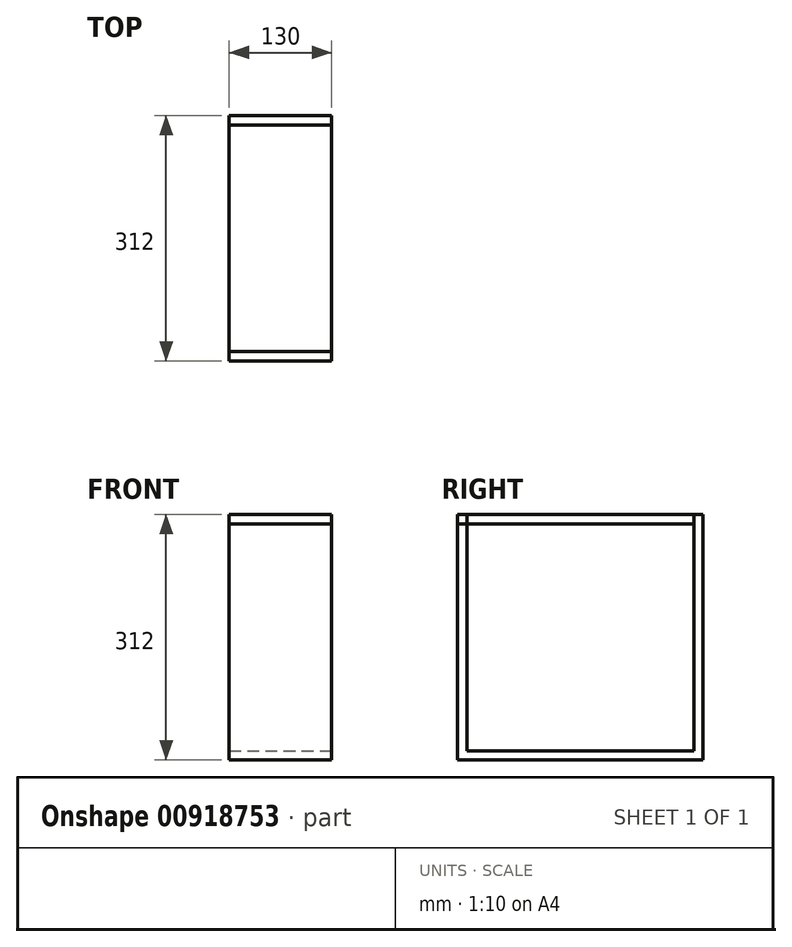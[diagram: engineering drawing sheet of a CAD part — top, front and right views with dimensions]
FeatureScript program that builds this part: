
annotation { "Feature Type Name" : "Feature", "Feature Type Description" : "" }
export const myFeature = defineFeature(function(context is Context, id is Id, definition is map)
    precondition{}
    {
        {
            var Q0;
            Q0=qCreatedBy(makeId("Top.planeOp"),FACE);
            var sketch = newSketch(context, id + "F0", { "sketchPlane" : qUnion([Q0])});
            skLineSegment(sketch, "E0.bottom", {"start": v(-937.94, -1757.44) * mm, "end": v(-807.94, -1757.44) * mm});
            skLineSegment(sketch, "E0.top", {"start": v(-937.94, -1769.44) * mm, "end": v(-807.94, -1769.44) * mm});
            skLineSegment(sketch, "E0.left", {"start": v(-937.94, -1757.44) * mm, "end": v(-937.94, -1769.44) * mm});
            skLineSegment(sketch, "E0.right", {"start": v(-807.94, -1757.44) * mm, "end": v(-807.94, -1769.44) * mm});
            skLineSegment(sketch, "E1.bottom", {"start": v(-937.94, -1469.44) * mm, "end": v(-807.94, -1469.44) * mm});
            skLineSegment(sketch, "E1.top", {"start": v(-937.94, -1457.44) * mm, "end": v(-807.94, -1457.44) * mm});
            skLineSegment(sketch, "E1.left", {"start": v(-937.94, -1457.44) * mm, "end": v(-937.94, -1469.44) * mm});
            skLineSegment(sketch, "E1.right", {"start": v(-807.94, -1457.44) * mm, "end": v(-807.94, -1469.44) * mm});
            skSolve(sketch);
        }
        {
            var Q0;
            Q0=makeQuery(id+"F0.imprint","IMPRINT",FACE,{"disambiguationData":[TD([[makeQuery(id+"F0.imprint","IMPRINT",EDGE,{"derivedFrom":sQuery(id+"F0.wireOp",EDGE,"E0.bottom")}),-1.0]])]});
            var Q1;
            Q1=makeQuery(id+"F0.imprint","IMPRINT",FACE,{"disambiguationData":[TD([[makeQuery(id+"F0.imprint","IMPRINT",EDGE,{"derivedFrom":sQuery(id+"F0.wireOp",EDGE,"E1.bottom")}),1.0]])]});
            extrude(context, id + "F1", {"entities" : qUnion([Q0, Q1]), "depth" : 300 * mm, "offsetDistance" : 25 * mm});
        }
        {
            var Q0;
            Q0=makeQuery(id+"F1.opExtrude","SWEPT_FACE",FACE,{"disambiguationData":[OSD([sQuery(id+"F0.wireOp",EDGE,"E1.bottom")])]});
            var sketch = newSketch(context, id + "F2", { "sketchPlane" : qUnion([Q0])});
            skLineSegment(sketch, "E2.bottom", {"start": v(-937.94, 300) * mm, "end": v(-807.94, 300) * mm});
            skLineSegment(sketch, "E2.top", {"start": v(-937.94, 288) * mm, "end": v(-807.94, 288) * mm});
            skLineSegment(sketch, "E2.left", {"start": v(-937.94, 300) * mm, "end": v(-937.94, 288) * mm});
            skLineSegment(sketch, "E2.right", {"start": v(-807.94, 300) * mm, "end": v(-807.94, 288) * mm});
            skSolve(sketch);
        }
        {
            var Q0;
            Q0 = qSketchRegion(id + "F2", true);
            extrude(context, id + "F3", {"entities" : qUnion([Q0]), "depth" : 300 * mm, "offsetDistance" : 25 * mm});
        }
        {
            var Q0;
            Q0=makeQuery(id+"F1.opExtrude","CAP_FACE",FACE,{"disambiguationData":[OSD([sQuery(id+"F0.wireOp",EDGE,"E0.bottom"),sQuery(id+"F0.wireOp",EDGE,"E0.top"),sQuery(id+"F0.wireOp",EDGE,"E0.left"),sQuery(id+"F0.wireOp",EDGE,"E0.right")])],"isStart":true});
            var sketch = newSketch(context, id + "F4", { "sketchPlane" : qUnion([Q0])});
            skLineSegment(sketch, "E3.bottom", {"start": v(-937.94, 1769.44) * mm, "end": v(-807.94, 1769.44) * mm});
            skLineSegment(sketch, "E3.top", {"start": v(-937.94, 1457.44) * mm, "end": v(-807.94, 1457.44) * mm});
            skLineSegment(sketch, "E3.left", {"start": v(-937.94, 1769.44) * mm, "end": v(-937.94, 1457.44) * mm});
            skLineSegment(sketch, "E3.right", {"start": v(-807.94, 1769.44) * mm, "end": v(-807.94, 1457.44) * mm});
            skSolve(sketch);
        }
        {
            var Q0;
            Q0 = qSketchRegion(id + "F4", true);
            extrude(context, id + "F5", {"entities" : qUnion([Q0]), "operationType" : NewBodyOperationType.ADD, "depth" : 12 * mm, "offsetDistance" : 25 * mm});
        }
    });
